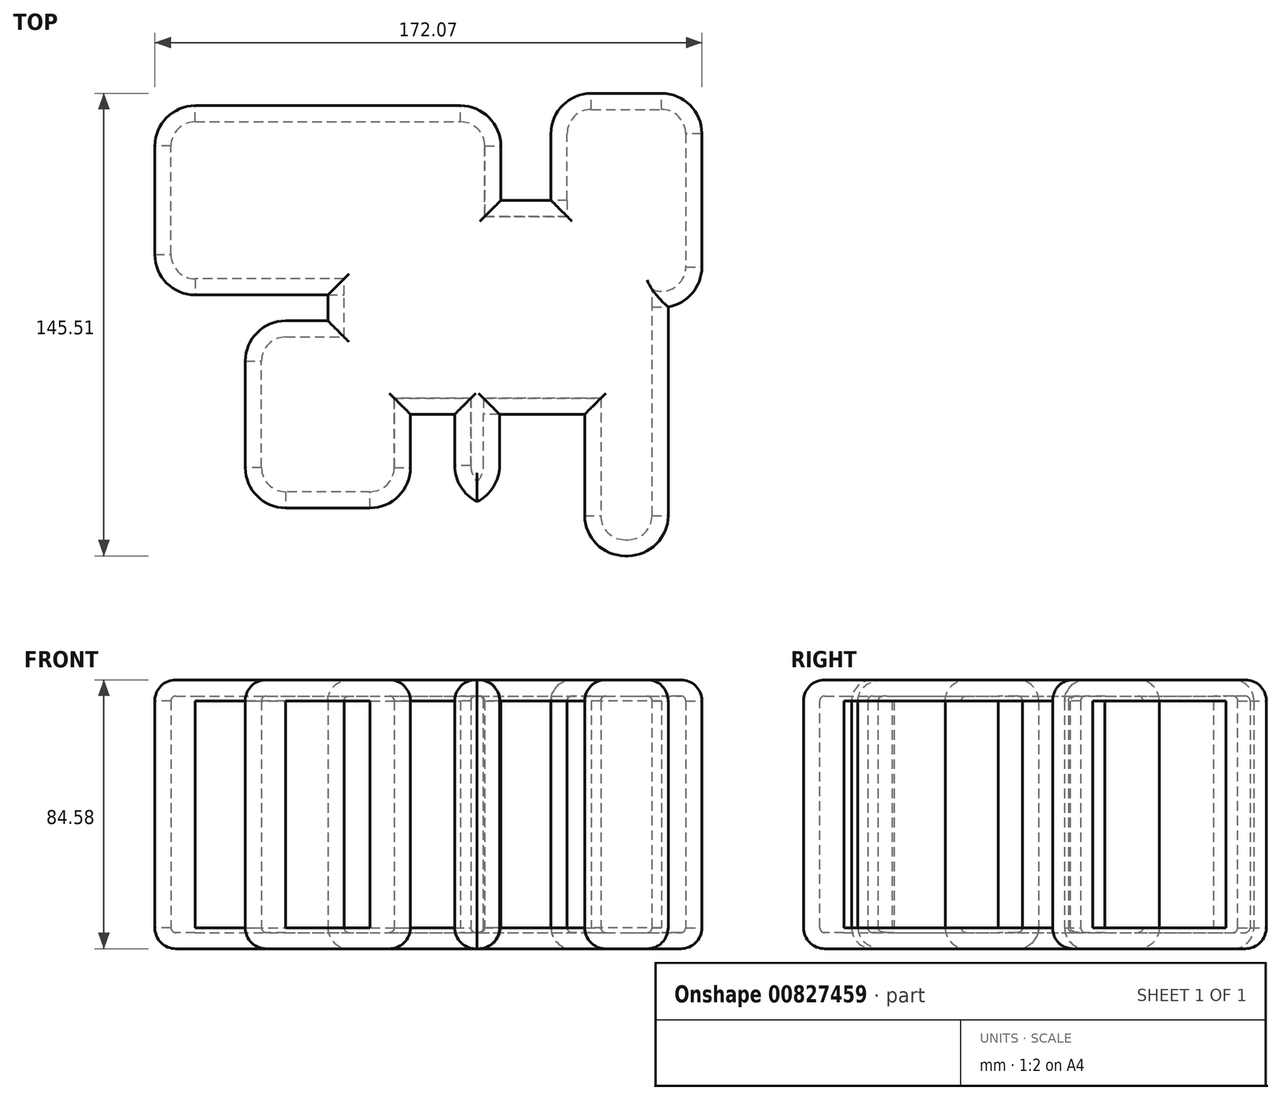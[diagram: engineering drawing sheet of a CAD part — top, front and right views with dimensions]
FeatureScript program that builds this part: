
annotation { "Feature Type Name" : "Feature", "Feature Type Description" : "" }
export const myFeature = defineFeature(function(context is Context, id is Id, definition is map)
    precondition{}
    {
        {
            var Q0;
            Q0=qCreatedBy(makeId("Top.planeOp"),FACE);
            var sketch = newSketch(context, id + "F0", { "sketchPlane" : qUnion([Q0])});
            skLineSegment(sketch, "E0.bottom", {"start": v(46.95, 33.67) * mm, "end": v(-46.95, 33.67) * mm});
            skLineSegment(sketch, "E0.top", {"start": v(46.95, -33.67) * mm, "end": v(-46.95, -33.67) * mm});
            skLineSegment(sketch, "E0.left", {"start": v(46.95, 33.67) * mm, "end": v(46.95, -33.67) * mm});
            skLineSegment(sketch, "E0.right", {"start": v(-46.95, 33.67) * mm, "end": v(-46.95, -33.67) * mm});
            skPoint(sketch, "E0.middle", {"position": v(0, 0) * mm});
            skLineSegment(sketch, "E1.bottom", {"start": v(57.99, 0) * mm, "end": v(23.22, 0) * mm});
            skLineSegment(sketch, "E1.top", {"start": v(57.99, 67.33) * mm, "end": v(35.92, 67.33) * mm});
            skLineSegment(sketch, "E1.left", {"start": v(70.69, 12.7) * mm, "end": v(70.69, 54.63) * mm});
            skLineSegment(sketch, "E1.right", {"start": v(23.22, 0) * mm, "end": v(23.22, 54.63) * mm});
            skPoint(sketch, "E1.middle", {"position": v(46.95, 33.67) * mm});
            skLineSegment(sketch, "E2.bottom", {"start": v(-88.68, 63.43) * mm, "end": v(-5.23, 63.43) * mm});
            skLineSegment(sketch, "E2.top", {"start": v(-88.68, 3.9) * mm, "end": v(7.47, 3.9) * mm});
            skLineSegment(sketch, "E2.left", {"start": v(-101.38, 50.73) * mm, "end": v(-101.38, 16.6) * mm});
            skLineSegment(sketch, "E2.right", {"start": v(7.47, 50.73) * mm, "end": v(7.47, 3.9) * mm});
            skPoint(sketch, "E2.middle", {"position": v(-46.95, 33.67) * mm});
            skLineSegment(sketch, "E3.bottom", {"start": v(-60.22, -63.08) * mm, "end": v(-33.69, -63.08) * mm});
            skLineSegment(sketch, "E3.top", {"start": v(-60.22, -4.25) * mm, "end": v(-33.69, -4.25) * mm});
            skLineSegment(sketch, "E3.left", {"start": v(-72.92, -50.38) * mm, "end": v(-72.92, -16.95) * mm});
            skLineSegment(sketch, "E3.right", {"start": v(-20.99, -50.38) * mm, "end": v(-20.99, -16.95) * mm});
            skPoint(sketch, "E3.middle", {"position": v(-46.95, -33.67) * mm});
            skLineSegment(sketch, "E4.bottom", {"start": v(46.52, -78.18) * mm, "end": v(47.39, -78.18) * mm});
            skLineSegment(sketch, "E4.top", {"start": v(33.82, 10.84) * mm, "end": v(60.09, 10.84) * mm});
            skLineSegment(sketch, "E4.left", {"start": v(33.82, -65.48) * mm, "end": v(33.82, 10.84) * mm});
            skLineSegment(sketch, "E4.right", {"start": v(60.09, -65.48) * mm, "end": v(60.09, 10.84) * mm});
            skPoint(sketch, "E4.middle", {"position": v(46.95, -33.67) * mm});
            skLineSegment(sketch, "E5.bottom", {"start": v(-5.63, -62.44) * mm, "end": v(5.63, -62.44) * mm});
            skLineSegment(sketch, "E5.top", {"start": v(-7.07, -4.9) * mm, "end": v(7.07, -4.9) * mm});
            skLineSegment(sketch, "E5.left", {"start": v(-7.07, -49.74) * mm, "end": v(-7.07, -4.9) * mm});
            skLineSegment(sketch, "E5.right", {"start": v(7.07, -49.74) * mm, "end": v(7.07, -4.9) * mm});
            skPoint(sketch, "E5.middle", {"position": v(0, -33.67) * mm});
            skPoint(sketch, "E6.visualSharp", {"position": v(-101.38, 63.43) * mm});
            skArc(sketch, "E6.filletArc", {"start": v(-88.68, 63.43) * mm, "mid": v(-97.66, 59.72) * mm, "end": v(-101.38, 50.73) * mm});
            skPoint(sketch, "E7.visualSharp", {"position": v(-101.38, 3.9) * mm});
            skArc(sketch, "E7.filletArc", {"start": v(-101.38, 16.6) * mm, "mid": v(-97.66, 7.62) * mm, "end": v(-88.68, 3.9) * mm});
            skPoint(sketch, "E8.visualSharp", {"position": v(-72.92, -4.25) * mm});
            skArc(sketch, "E8.filletArc", {"start": v(-60.22, -4.25) * mm, "mid": v(-69.2, -7.97) * mm, "end": v(-72.92, -16.95) * mm});
            skPoint(sketch, "E9.visualSharp", {"position": v(-72.92, -63.08) * mm});
            skArc(sketch, "E9.filletArc", {"start": v(-72.92, -50.38) * mm, "mid": v(-69.2, -59.36) * mm, "end": v(-60.22, -63.08) * mm});
            skPoint(sketch, "E10.visualSharp", {"position": v(-20.99, -63.08) * mm});
            skArc(sketch, "E10.filletArc", {"start": v(-33.69, -63.08) * mm, "mid": v(-24.7, -59.36) * mm, "end": v(-20.99, -50.38) * mm});
            skPoint(sketch, "E11.visualSharp", {"position": v(-20.99, -4.25) * mm});
            skArc(sketch, "E11.filletArc", {"start": v(-20.99, -16.95) * mm, "mid": v(-24.7, -7.97) * mm, "end": v(-33.69, -4.25) * mm});
            skPoint(sketch, "E12.visualSharp", {"position": v(-7.07, -62.44) * mm});
            skArc(sketch, "E12.filletArc", {"start": v(-7.07, -49.74) * mm, "mid": v(-3.35, -58.72) * mm, "end": v(5.63, -62.44) * mm});
            skPoint(sketch, "E13.visualSharp", {"position": v(7.07, -62.44) * mm});
            skArc(sketch, "E13.filletArc", {"start": v(-5.63, -62.44) * mm, "mid": v(3.35, -58.72) * mm, "end": v(7.07, -49.74) * mm});
            skPoint(sketch, "E14.visualSharp", {"position": v(33.82, -78.18) * mm});
            skArc(sketch, "E14.filletArc", {"start": v(33.82, -65.48) * mm, "mid": v(37.54, -74.46) * mm, "end": v(46.52, -78.18) * mm});
            skPoint(sketch, "E15.visualSharp", {"position": v(60.09, -78.18) * mm});
            skArc(sketch, "E15.filletArc", {"start": v(47.39, -78.18) * mm, "mid": v(56.37, -74.46) * mm, "end": v(60.09, -65.48) * mm});
            skPoint(sketch, "E16.visualSharp", {"position": v(70.69, 0) * mm});
            skArc(sketch, "E16.filletArc", {"start": v(57.99, 0) * mm, "mid": v(66.97, 3.72) * mm, "end": v(70.69, 12.7) * mm});
            skPoint(sketch, "E17.visualSharp", {"position": v(70.69, 67.33) * mm});
            skArc(sketch, "E17.filletArc", {"start": v(70.69, 54.63) * mm, "mid": v(66.97, 63.61) * mm, "end": v(57.99, 67.33) * mm});
            skPoint(sketch, "E18.visualSharp", {"position": v(23.22, 67.33) * mm});
            skArc(sketch, "E18.filletArc", {"start": v(35.92, 67.33) * mm, "mid": v(26.94, 63.61) * mm, "end": v(23.22, 54.63) * mm});
            skPoint(sketch, "E19.visualSharp", {"position": v(7.47, 63.43) * mm});
            skArc(sketch, "E19.filletArc", {"start": v(7.47, 50.73) * mm, "mid": v(3.75, 59.72) * mm, "end": v(-5.23, 63.43) * mm});
            skSolve(sketch);
        }
        {
            var Q0;
            Q0=makeQuery(id+"F0.imprint","IMPRINT",FACE,{"disambiguationData":[TD([[makeQuery(id+"F0.imprint","IMPRINT",EDGE,{"derivedFrom":sQuery(id+"F0.wireOp",EDGE,"E3.bottom")}),1.0]])]});
            var Q1;
            Q1=makeQuery(id+"F0.imprint","IMPRINT",FACE,{"disambiguationData":[TD([[makeQuery(id+"F0.imprint","IMPRINT",EDGE,{"derivedFrom":sQuery(id+"F0.wireOp",EDGE,"E2.bottom")}),-1.0]])]});
            var Q2;
            {var subQ0=sQuery(id+"F0.wireOp",EDGE,"E0.right");var subQ1=sQuery(id+"F0.wireOp",EDGE,"E0.bottom");var subQ2=makeQuery(id+"F0.imprint","INTERSECT",VERTEX,{"derivedFrom":[subQ1,subQ0]});Q2=makeQuery(id+"F0.imprint","IMPRINT",FACE,{"disambiguationData":[TD([[makeQuery(id+"F0.imprint","IMPRINT",EDGE,{"disambiguationData":[TD([[subQ2,1.0]])],"derivedFrom":subQ1}),1.0]])]});}
            var Q3;
            {var subQ0=sQuery(id+"F0.wireOp",EDGE,"E11.filletArc");Q3=makeQuery(id+"F0.imprint","IMPRINT",FACE,{"disambiguationData":[TD([[makeQuery(id+"F0.imprint","IMPRINT",EDGE,{"derivedFrom":subQ0}),1.0]])]});}
            var Q4;
            {var subQ14=sQuery(id+"F0.wireOp",EDGE,"E5.top");Q4=makeQuery(id+"F0.imprint","IMPRINT",FACE,{"disambiguationData":[TD([[makeQuery(id+"F0.imprint","IMPRINT",EDGE,{"derivedFrom":subQ14}),1.0]])]});}
            var Q5;
            {var subQ5=sQuery(id+"F0.wireOp",EDGE,"E5.top");Q5=makeQuery(id+"F0.imprint","IMPRINT",FACE,{"disambiguationData":[TD([[makeQuery(id+"F0.imprint","IMPRINT",EDGE,{"derivedFrom":subQ5}),-1.0]])]});}
            var Q6;
            {var subQ5=sQuery(id+"F0.wireOp",EDGE,"E0.top");var subQ7=sQuery(id+"F0.wireOp",EDGE,"E5.right");var subQ9=makeQuery(id+"F0.imprint","INTERSECT",VERTEX,{"derivedFrom":[subQ5,subQ7]});Q6=makeQuery(id+"F0.imprint","IMPRINT",FACE,{"disambiguationData":[TD([[makeQuery(id+"F0.imprint","IMPRINT",EDGE,{"disambiguationData":[TD([[subQ9,-1.0]])],"derivedFrom":subQ5}),1.0]])]});}
            var Q7;
            Q7=makeQuery(id+"F0.imprint","IMPRINT",FACE,{"disambiguationData":[TD([[makeQuery(id+"F0.imprint","IMPRINT",EDGE,{"derivedFrom":sQuery(id+"F0.wireOp",EDGE,"E4.bottom")}),1.0]])]});
            var Q8;
            {var subQ0=sQuery(id+"F0.wireOp",EDGE,"E0.left");var subQ1=sQuery(id+"F0.wireOp",EDGE,"E0.top");var subQ2=makeQuery(id+"F0.imprint","INTERSECT",VERTEX,{"derivedFrom":[subQ1,subQ0]});Q8=makeQuery(id+"F0.imprint","IMPRINT",FACE,{"disambiguationData":[TD([[makeQuery(id+"F0.imprint","IMPRINT",EDGE,{"disambiguationData":[TD([[subQ2,-1.0]])],"derivedFrom":subQ1}),-1.0]])]});}
            var Q9;
            {var subQ0=sQuery(id+"F0.wireOp",EDGE,"E4.top");var subQ1=sQuery(id+"F0.wireOp",EDGE,"E0.left");var subQ2=makeQuery(id+"F0.imprint","INTERSECT",VERTEX,{"derivedFrom":[subQ1,subQ0]});Q9=makeQuery(id+"F0.imprint","IMPRINT",FACE,{"disambiguationData":[TD([[makeQuery(id+"F0.imprint","IMPRINT",EDGE,{"disambiguationData":[TD([[subQ2,-1.0]])],"derivedFrom":subQ1}),-1.0]])]});}
            var Q10;
            {var subQ3=sQuery(id+"F0.wireOp",EDGE,"E0.bottom");var subQ5=sQuery(id+"F0.wireOp",EDGE,"E0.left");var subQ6=makeQuery(id+"F0.imprint","INTERSECT",VERTEX,{"derivedFrom":[subQ3,subQ5]});Q10=makeQuery(id+"F0.imprint","IMPRINT",FACE,{"disambiguationData":[TD([[makeQuery(id+"F0.imprint","IMPRINT",EDGE,{"disambiguationData":[TD([[subQ6,-1.0]])],"derivedFrom":subQ3}),1.0]])]});}
            var Q11;
            {var subQ1=sQuery(id+"F0.wireOp",EDGE,"E4.top");var subQ5=sQuery(id+"F0.wireOp",EDGE,"E0.left");var subQ6=makeQuery(id+"F0.imprint","INTERSECT",VERTEX,{"derivedFrom":[subQ5,subQ1]});Q11=makeQuery(id+"F0.imprint","IMPRINT",FACE,{"disambiguationData":[TD([[makeQuery(id+"F0.imprint","IMPRINT",EDGE,{"disambiguationData":[TD([[subQ6,-1.0]])],"derivedFrom":subQ5}),1.0]])]});}
            var Q12;
            Q12=makeQuery(id+"F0.imprint","IMPRINT",FACE,{"disambiguationData":[TD([[makeQuery(id+"F0.imprint","IMPRINT",EDGE,{"derivedFrom":sQuery(id+"F0.wireOp",EDGE,"E1.top")}),1.0]])]});
            extrude(context, id + "F1", {"entities" : qUnion([Q0, Q1, Q2, Q3, Q4, Q5, Q6, Q7, Q8, Q9, Q10, Q11, Q12]), "depth" : 84.58 * mm, "offsetDistance" : 25.4 * mm});
        }
        {
            var Q0;
            Q0=makeQuery(id+"F1.opExtrude","CAP_FACE",FACE,{"disambiguationData":[OSD([sQuery(id+"F0.wireOp",EDGE,"E0.bottom"),sQuery(id+"F0.wireOp",EDGE,"E0.top"),sQuery(id+"F0.wireOp",EDGE,"E0.right"),sQuery(id+"F0.wireOp",EDGE,"E1.top"),sQuery(id+"F0.wireOp",EDGE,"E1.left"),sQuery(id+"F0.wireOp",EDGE,"E1.right"),sQuery(id+"F0.wireOp",EDGE,"E2.bottom"),sQuery(id+"F0.wireOp",EDGE,"E2.top"),sQuery(id+"F0.wireOp",EDGE,"E2.left"),sQuery(id+"F0.wireOp",EDGE,"E2.right"),sQuery(id+"F0.wireOp",EDGE,"E3.bottom"),sQuery(id+"F0.wireOp",EDGE,"E3.top"),sQuery(id+"F0.wireOp",EDGE,"E3.left"),sQuery(id+"F0.wireOp",EDGE,"E3.right"),sQuery(id+"F0.wireOp",EDGE,"E4.bottom"),sQuery(id+"F0.wireOp",EDGE,"E4.left"),sQuery(id+"F0.wireOp",EDGE,"E4.right"),sQuery(id+"F0.wireOp",EDGE,"E5.left"),sQuery(id+"F0.wireOp",EDGE,"E5.right"),sQuery(id+"F0.wireOp",EDGE,"E6.filletArc"),sQuery(id+"F0.wireOp",EDGE,"E7.filletArc"),sQuery(id+"F0.wireOp",EDGE,"E8.filletArc"),sQuery(id+"F0.wireOp",EDGE,"E9.filletArc"),sQuery(id+"F0.wireOp",EDGE,"E10.filletArc"),sQuery(id+"F0.wireOp",EDGE,"E12.filletArc"),sQuery(id+"F0.wireOp",EDGE,"E13.filletArc"),sQuery(id+"F0.wireOp",EDGE,"E14.filletArc"),sQuery(id+"F0.wireOp",EDGE,"E15.filletArc"),sQuery(id+"F0.wireOp",EDGE,"E16.filletArc"),sQuery(id+"F0.wireOp",EDGE,"E17.filletArc"),sQuery(id+"F0.wireOp",EDGE,"E18.filletArc"),sQuery(id+"F0.wireOp",EDGE,"E19.filletArc")])],"isStart":false});
            var Q1;
            Q1=makeQuery(id+"F1.opExtrude","CAP_FACE",FACE,{"disambiguationData":[OSD([sQuery(id+"F0.wireOp",EDGE,"E0.bottom"),sQuery(id+"F0.wireOp",EDGE,"E0.top"),sQuery(id+"F0.wireOp",EDGE,"E0.right"),sQuery(id+"F0.wireOp",EDGE,"E1.top"),sQuery(id+"F0.wireOp",EDGE,"E1.left"),sQuery(id+"F0.wireOp",EDGE,"E1.right"),sQuery(id+"F0.wireOp",EDGE,"E2.bottom"),sQuery(id+"F0.wireOp",EDGE,"E2.top"),sQuery(id+"F0.wireOp",EDGE,"E2.left"),sQuery(id+"F0.wireOp",EDGE,"E2.right"),sQuery(id+"F0.wireOp",EDGE,"E3.bottom"),sQuery(id+"F0.wireOp",EDGE,"E3.top"),sQuery(id+"F0.wireOp",EDGE,"E3.left"),sQuery(id+"F0.wireOp",EDGE,"E3.right"),sQuery(id+"F0.wireOp",EDGE,"E4.bottom"),sQuery(id+"F0.wireOp",EDGE,"E4.left"),sQuery(id+"F0.wireOp",EDGE,"E4.right"),sQuery(id+"F0.wireOp",EDGE,"E5.left"),sQuery(id+"F0.wireOp",EDGE,"E5.right"),sQuery(id+"F0.wireOp",EDGE,"E6.filletArc"),sQuery(id+"F0.wireOp",EDGE,"E7.filletArc"),sQuery(id+"F0.wireOp",EDGE,"E8.filletArc"),sQuery(id+"F0.wireOp",EDGE,"E9.filletArc"),sQuery(id+"F0.wireOp",EDGE,"E10.filletArc"),sQuery(id+"F0.wireOp",EDGE,"E12.filletArc"),sQuery(id+"F0.wireOp",EDGE,"E13.filletArc"),sQuery(id+"F0.wireOp",EDGE,"E14.filletArc"),sQuery(id+"F0.wireOp",EDGE,"E15.filletArc"),sQuery(id+"F0.wireOp",EDGE,"E16.filletArc"),sQuery(id+"F0.wireOp",EDGE,"E17.filletArc"),sQuery(id+"F0.wireOp",EDGE,"E18.filletArc"),sQuery(id+"F0.wireOp",EDGE,"E19.filletArc")])],"isStart":true});
            fillet(context, id + "F2", {"entities" : qUnion([Q0, Q1]), "radius" : 6.6 * mm, "tangentPropagation" : true, "allowEdgeOverflow" : false});
        }
        {
            var Q0;
            Q0=makeQuery(id+"F1.opExtrude","SWEPT_FACE",FACE,{"disambiguationData":[OSD([sQuery(id+"F0.wireOp",EDGE,"E2.top")])]});
            var Q1;
            Q1=makeQuery(id+"F1.opExtrude","SWEPT_FACE",FACE,{"disambiguationData":[OSD([sQuery(id+"F0.wireOp",EDGE,"E2.left")])]});
            var Q2;
            Q2=makeQuery(id+"F1.opExtrude","SWEPT_FACE",FACE,{"disambiguationData":[OSD([sQuery(id+"F0.wireOp",EDGE,"E3.bottom")])]});
            var Q3;
            Q3=makeQuery(id+"F1.opExtrude","SWEPT_FACE",FACE,{"disambiguationData":[OSD([sQuery(id+"F0.wireOp",EDGE,"E3.left")])]});
            var Q4;
            Q4=makeQuery(id+"F1.opExtrude","SWEPT_FACE",FACE,{"disambiguationData":[OSD([sQuery(id+"F0.wireOp",EDGE,"E3.right")])]});
            var Q5;
            Q5=makeQuery(id+"F1.opExtrude","SWEPT_FACE",FACE,{"disambiguationData":[OSD([sQuery(id+"F0.wireOp",EDGE,"E5.left")])]});
            var Q6;
            {var subQ0=sQuery(id+"F0.wireOp",EDGE,"E0.top");Q6=makeQuery(id+"F1.opExtrude","SWEPT_FACE",FACE,{"disambiguationData":[OSD([subQ0]),TDD([makeQuery(id+"F0.imprint","IMPRINT",EDGE,{"disambiguationData":[TD([[makeQuery(id+"F0.imprint","INTERSECT",VERTEX,{"derivedFrom":[subQ0,sQuery(id+"F0.wireOp",EDGE,"E4.left")]}),-1.0]])],"derivedFrom":subQ0})])]});}
            var Q7;
            {var subQ0=sQuery(id+"F0.wireOp",EDGE,"E0.top");Q7=makeQuery(id+"F1.opExtrude","SWEPT_FACE",FACE,{"disambiguationData":[OSD([subQ0]),TDD([makeQuery(id+"F0.imprint","IMPRINT",EDGE,{"disambiguationData":[TD([[makeQuery(id+"F0.imprint","INTERSECT",VERTEX,{"derivedFrom":[subQ0,sQuery(id+"F0.wireOp",EDGE,"E5.left")]}),-1.0]])],"derivedFrom":subQ0})])]});}
            var Q8;
            Q8=makeQuery(id+"F1.opExtrude","SWEPT_FACE",FACE,{"disambiguationData":[OSD([sQuery(id+"F0.wireOp",EDGE,"E4.left")])]});
            var Q9;
            Q9=makeQuery(id+"F1.opExtrude","SWEPT_FACE",FACE,{"disambiguationData":[OSD([sQuery(id+"F0.wireOp",EDGE,"E1.left")])]});
            var Q10;
            Q10=makeQuery(id+"F1.opExtrude","SWEPT_FACE",FACE,{"disambiguationData":[OSD([sQuery(id+"F0.wireOp",EDGE,"E0.bottom")])]});
            var Q11;
            Q11=makeQuery(id+"F1.opExtrude","SWEPT_FACE",FACE,{"disambiguationData":[OSD([sQuery(id+"F0.wireOp",EDGE,"E2.right")])]});
            shell(context, id + "F3", {"entities" : qUnion([Q0, Q1, Q2, Q3, Q4, Q5, Q6, Q7, Q8, Q9, Q10, Q11]), "thickness" : 5.08 * mm});
        }
        {
            var Q0;
            Q0=makeQuery(id+"F1.opExtrude","SWEPT_FACE",FACE,{"disambiguationData":[OSD([sQuery(id+"F0.wireOp",EDGE,"E1.top")])]});
            var Q1;
            Q1=makeQuery(id+"F1.opExtrude","SWEPT_FACE",FACE,{"disambiguationData":[OSD([sQuery(id+"F0.wireOp",EDGE,"E2.bottom")])]});
            extrude(context, id + "F4", {"entities" : qUnion([Q0, Q1]), "operationType" : NewBodyOperationType.REMOVE, "oppositeDirection" : true, "depth" : 25.4 * mm, "offsetDistance" : 25.4 * mm});
        }
        {
            var Q0;
            Q0=makeQuery(id+"F1.opExtrude","SWEPT_FACE",FACE,{"disambiguationData":[OSD([sQuery(id+"F0.wireOp",EDGE,"E4.right")])]});
            extrude(context, id + "F5", {"entities" : qUnion([Q0]), "operationType" : NewBodyOperationType.REMOVE, "oppositeDirection" : true, "depth" : 25.4 * mm, "offsetDistance" : 25.4 * mm});
        }
    });
